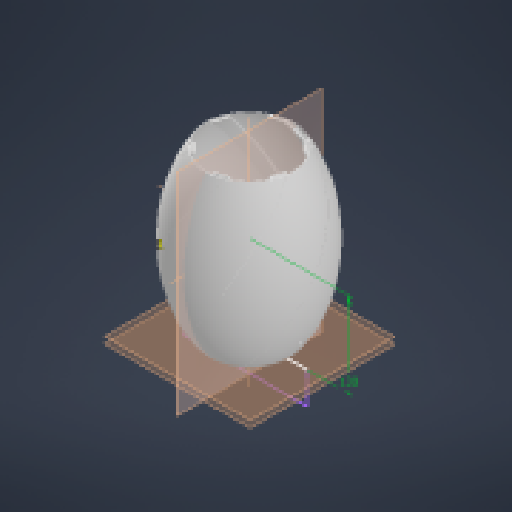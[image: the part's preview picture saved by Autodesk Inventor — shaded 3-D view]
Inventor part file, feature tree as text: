
AUTODESK INVENTOR PART (.ipt)
format: ipt  version: 2023 (Build 270158000, 158)  size: 4,185,088 bytes
history: native  units: mm
features: sketch x13, extrude x8, projected_geometry x6, plane x5, other x5, pattern_circular x4, revolve x2, sweep x1, chamfer x1, shell x1, reference x1
ambient origin geometry x8: Origin, YZ Plane, XZ Plane, XY Plane, X Axis, Y Axis, Z Axis, Center Point
bodies: Solid1 (feature_tree)
feature tree (47):
  revolve  "Revolution1"  [1 undecoded]
  sketch  "3D Sketch1"
  plane  "Work Plane1"
  sweep  "Sweep1"
  pattern_circular  "Circular Pattern1"  Count=6 Angle=360.0deg
  extrude  "Extrusion1"  TaperAngle=0.0deg  [1 undecoded]
  plane  "Work Plane3"
  sketch  "Sketch12"  dims[d16=0.2mm]
  plane  "Work Plane6"
  extrude  "Extrusion6"  Depth=1.0mm
  chamfer  "Chamfer2"  Distance=10.0mm
  pattern_circular  "Circular Pattern4"  [2 undecoded]
  shell  "Shell2"  Thickness=4.0mm
  sketch  "Sketch16"  dims[d26=-130.0mm d27=-10.0mm d29=1.0mm d30=10.0mm d31=0.0mm d32=6.0mm d33=4.0mm d34=0.0mm d35=4.0mm d36=4.0mm d37=0.0mm d38=30.0mm d39=360.0deg d51=100.0mm d52=6.0mm d53=4.0mm d54=0.0mm d55=3.5mm d56=1.0mm d57=45.0deg d58=30.0mm d59=360.0deg d61=30.0deg d62=6.0mm d63=4.0mm d64=0.0mm d65=60.0mm d66=360.0deg d68=360.0deg d69=130.0mm d70=0.0mm d71=0.0mm d72=0.0mm d73=0.0mm]
  extrude  "Extrusion8"  Depth=4.0mm
  extrude  "Extrusion2"  Depth=4.0mm TaperAngle=0.0deg
  sketch  "Sketch7"  dims[d13=1.6mm]
  plane  "Work Plane4"
  extrude  "Extrusion3"  Depth=30.0mm TaperAngle=360.0deg
  extrude  "Extrusion4"  Depth=100.0mm
  pattern_circular  "Circular Pattern2"  [2 undecoded]
  extrude  "Extrusion7"  Depth=4.0mm TaperAngle=0.0deg
  pattern_circular  "Circular Pattern5"  Angle=45.0deg  [1 undecoded]
  revolve  "Revolution2"  Angle=360.0deg
  extrude  "Extrusion9"  TaperAngle=30.0deg  [1 undecoded]
  sketch  "Sketch1"  dims[d0=160.0mm d1=100.0mm]
  other  "Helical Curve2"
  other  "Project to Surface1"
  sketch  "Sketch2"  dims[d2=90.0deg d7=1200.0mm d8=637.649mm d9=252.623mm d10=0.0mm]
  sketch  "Sketch3"  dims[d11=15.0mm]
  plane  "Work Plane2"
  sketch  "Sketch6"  dims[d12=3.0mm]
  sketch  "Sketch8"  dims[d14=1.478932mm]
  sketch  "Sketch9"  dims[d15=0.2mm]
  sketch  "Sketch13"  dims[d17=0.2mm]
  sketch  "Sketch14"  dims[d18=0.0mm d19=0.0mm d20=60.0mm d21=360.0deg]
  reference  "Reference1"
  sketch  "Sketch15"  dims[d23=120.0mm d24=0.0mm d25=0.0mm]
  projected_geometry  "Project Cut Edges1"
  projected_geometry  "Project Cut Edges2"
  projected_geometry  "Project Cut Edges3"
  projected_geometry  "Project Cut Edges5"
  projected_geometry  "Project Cut Edges6"
  parser-record x1  (decoder bookkeeping rows leaked as tree rows — omitted from the tree; the rows remain in map.json)
  other  "assembly.iam"
  other  "ring_unten:1"
  projected_geometry  "Project Cut Edges7"
note: 8 required parameter values undecoded (feature->parameter linkage not recoverable at this tier; creation-order binding heuristic only, values carry confidence <= 0.55)
note: 1 file-system path scrubbed to <path> (originals preserved in map.json)